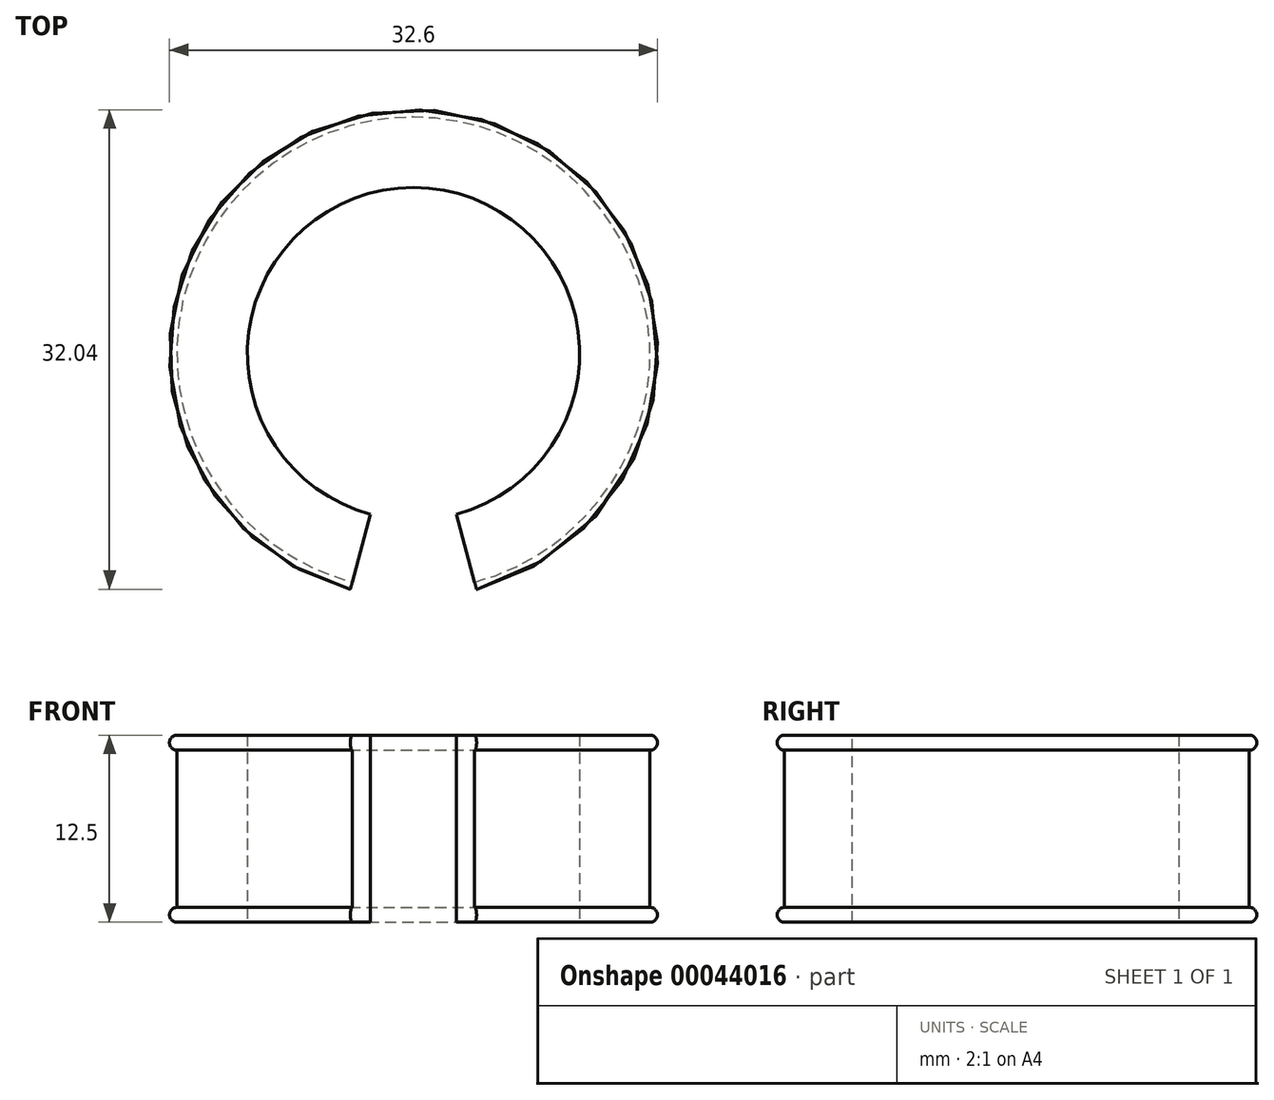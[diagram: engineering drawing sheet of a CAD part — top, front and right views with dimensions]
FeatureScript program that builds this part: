
annotation { "Feature Type Name" : "Feature", "Feature Type Description" : "" }
export const myFeature = defineFeature(function(context is Context, id is Id, definition is map)
    precondition{}
    {
        {
            var Q0;
            Q0=qCreatedBy(makeId("Right.planeOp"),FACE);
            var sketch = newSketch(context, id + "F0", { "sketchPlane" : qUnion([Q0])});
            skLineSegment(sketch, "E0", {"start": v(0, 0) * mm, "end": v(0, 12.5) * mm, "construction": true});
            skLineSegment(sketch, "E1.bottom", {"start": v(11.1, 0) * mm, "end": v(15.8, 0) * mm});
            skLineSegment(sketch, "E1.top", {"start": v(11.1, 12.5) * mm, "end": v(15.8, 12.5) * mm});
            skLineSegment(sketch, "E1.left", {"start": v(11.1, 0) * mm, "end": v(11.1, 12.5) * mm});
            skLineSegment(sketch, "E1.right", {"start": v(15.8, 1) * mm, "end": v(15.8, 11.5) * mm});
            skArc(sketch, "E2", {"start": v(15.8, 12.5) * mm, "mid": v(16.3, 12) * mm, "end": v(15.8, 11.5) * mm});
            skArc(sketch, "E3", {"start": v(15.8, 0) * mm, "mid": v(16.3, 0.5) * mm, "end": v(15.8, 1) * mm});
            skSolve(sketch);
        }
        {
            var Q0;
            Q0=makeQuery(id+"F0.imprint","IMPRINT",FACE,{"disambiguationData":[TD([[makeQuery(id+"F0.imprint","IMPRINT",EDGE,{"derivedFrom":sQuery(id+"F0.wireOp",EDGE,"E1.bottom")}),1.0]])]});
            var Q1;
            Q1=sQuery(id+"F0.wireOp",EDGE,"E0");
            revolve(context, id + "F1", {"entities" : qUnion([Q0]), "axis" : qUnion([Q1]), "revolveType" : RevolveType.SYMMETRIC, "angle" : 330 * degree});
        }
    });
